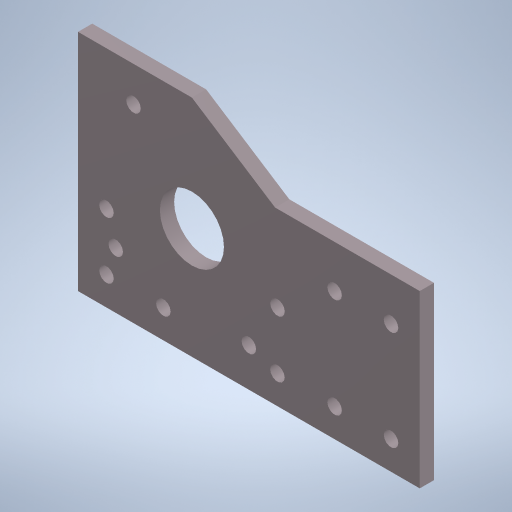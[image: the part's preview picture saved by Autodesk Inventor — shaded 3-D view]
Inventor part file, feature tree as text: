
AUTODESK INVENTOR PART (.ipt)
format: ipt  version: 2023.2 (Build 272271000, 271)  size: 467,456 bytes
history: native  units: mm
features: reference x26, other x5, sketch x3, extrude x2, plane x1, hole x1
ambient origin geometry x8: Origin, YZ Plane, XZ Plane, XY Plane, X Axis, Y Axis, Z Axis, Center Point
bodies: Solid1 (feature_tree)
feature tree (38):
  plane  "Work Plane1"
  extrude  "Extrusion1"  Depth=5.1mm
  hole  "Hole3"  [1 undecoded]
  extrude  "Extrusion2"  Depth=5.0mm
  sketch  "Sketch1"  dims[d0=5.1mm d2=5.1mm]
  reference  "Reference1"
  reference  "Reference2"
  reference  "Reference3"
  reference  "Reference4"
  reference  "Reference5"
  reference  "Reference6"
  reference  "Reference7"
  reference  "Reference8"
  reference  "Reference9"
  reference  "Reference10"
  reference  "Reference11"
  reference  "Reference12"
  reference  "Reference13"
  reference  "Reference14"
  reference  "Reference15"
  reference  "Reference16"
  reference  "Reference17"
  reference  "Reference18"
  reference  "Reference19"
  reference  "Reference20"
  reference  "Reference21"
  reference  "Reference22"
  reference  "Reference23"
  reference  "Reference24"
  reference  "Reference25"
  sketch  "Sketch6"  dims[d9=5.1mm d10=15.0mm]
  sketch  "Sketch7"  dims[d11=15.0mm d17=47.15mm d22=5.0mm d23=5.0mm d24=5.0mm d27=5.0mm d28=0.0mm d29=20.0mm d30=7.0mm d31=47.15mm d32=22.1mm d33=5.1mm d34=5.1mm d35=5.1mm d36=5.1mm d37=5.1mm d52=5.1mm d53=6.0mm d54=4.0mm d55=2.0mm d56=90.0deg d57=8.0mm d58=20.594885mm d59=22.5mm d60=5.0mm d61=0.0mm]
  reference  "Reference26"
  parser-record x1  (decoder bookkeeping rows leaked as tree rows — omitted from the tree; the rows remain in map.json)
  other  "Main Assembly.iam"
  other  "C beam extrusion 250:2"
  other  "20x40 1000:1"
  other  "ACME-Nut-Block:1"
note: 1 required parameter value undecoded (feature->parameter linkage not recoverable at this tier; creation-order binding heuristic only, values carry confidence <= 0.55)
note: 1 file-system path scrubbed to <path> (originals preserved in map.json)
